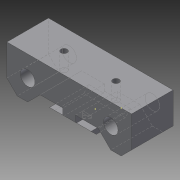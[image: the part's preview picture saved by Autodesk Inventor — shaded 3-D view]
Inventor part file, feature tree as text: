
AUTODESK INVENTOR PART (.ipt)
format: ipt  version: 2015 (Build 190159000, 159)  size: 163,840 bytes
history: native  units: mm
features: sketch x8, extrude x5, chamfer x3, hole x1
ambient origin geometry x8: Origin, YZ Plane, XZ Plane, XY Plane, X Axis, Y Axis, Z Axis, Center Point
bodies: Solid1 (feature_tree)
feature tree (17):
  extrude  "Extrusion1"  Depth=20.0mm
  extrude  "Extrusion2"  Depth=40.0mm
  hole  "Hole1"  [1 undecoded]
  extrude  "Extrusion3"  Depth=7.0mm
  chamfer  "Chamfer1"  Distance=20.0mm
  sketch  "Sketch5"  dims[d9=7.0mm d10=20.0mm d11=0.0mm]
  sketch  "Sketch6"  dims[d12=10.0mm d13=10.0mm]
  extrude  "Extrusion4"  Depth=10.0mm
  chamfer  "Chamfer2"  Distance=17.5mm
  chamfer  "Chamfer3"  Distance=16.0mm
  extrude  "Extrusion5"  Depth=1.0mm
  sketch  "Sketch1"  dims[d0=60.0mm d1=20.0mm]
  sketch  "Sketch2"  dims[d2=20.0mm d3=0.0mm d4=40.0mm]
  sketch  "Sketch3"  dims[d5=10.0mm d6=10.0mm]
  sketch  "Sketch4"  dims[d7=10.0mm d8=7.0mm]
  sketch  "Sketch7"  dims[d14=25.0mm]
  sketch  "Sketch8"  dims[d15=17.5mm d16=17.5mm d17=3.0mm d18=6.0mm d19=4.0mm d20=2.0mm d21=90.0deg d22=8.0mm d23=20.594885mm d24=16.0mm d25=16.0mm d26=6.0mm d27=20.0mm d28=0.0mm d29=6.0mm d30=2.0mm d31=45.0deg d32=20.0mm d33=20.0mm d34=2.5mm d35=7.0mm d36=7.0mm d37=20.0mm d38=0.0mm d39=3.0mm d40=2.0mm d41=45.0deg d42=5.0mm d43=2.0mm d44=45.0deg d45=3.0mm d46=45.0deg d47=1.0mm d48=0.0mm]
note: 1 required parameter value undecoded (feature->parameter linkage not recoverable at this tier; creation-order binding heuristic only, values carry confidence <= 0.55)
